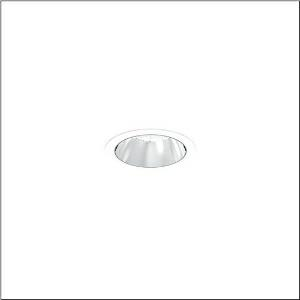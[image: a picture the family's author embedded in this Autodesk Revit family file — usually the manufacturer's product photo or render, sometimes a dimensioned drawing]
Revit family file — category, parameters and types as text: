
# Revit family: lunis_21_m_51db15mc91c
name_source: partatom
category: Lighting Fixtures
units: mm (PartAtom-declared; Revit-internal decimal feet)

## family parameters
Cut with Voids When Loaded = No
Host = Face
Light Source = No
Part Type = Normal
Room Calculation Point = No
Round Connector Dimension = Use Diameter
Shared = No

## types (1)
- --- (1 x LED, 4040 lm, 25.5 W, 6500K)
    Apparent Load = 26 VA
    CIE Flux Codes = 95 99 100 100 100
    Color Rendering = 80
    Color Temperature = 6500K
    Default Elevation = 1800 mm
    Description = Lunis 21,  M, downlight, light control with lens, of PMMA, anti glare with reflector, of PC, highly specular, light emission: direct distribution, LED rated luminous flux: 1.860lm, light colour: 830/840/865, with terminal, 3-pole, mains connection: 220..240V, AC/DC, 0/50..60Hz, housing, round, of diecast aluminium, traffic white (RAL 9016), diameter: 115mm, clamping range: 1..40mm, protection rating (complete): IP20, protection rating (on room side): IP54, insulation class (complete): insulation class II (safety insulation), certification: CE, impact resistance: IK03, packaging unit: 1 piece
    Height = 0 mm  [stored 0 ft]
    Lamp = 1 x LED
    Lamp Light Flux = 4040 lm
    Lamp Power = 25.5 W
    Lamp count = 1
    Length = 115 mm
    Luminous efficacy = 158 lm/W
    Manufacturer = Siteco
    ModVariant = No
    Model = 51DB15MC91C
    Mounting Place = Ceiling
    Mounting Type = Recessed
    Number of Poles = 1
    OnlyDefault = Yes
    Power Factor = 1
    Product Name = Lunis 21 M
    Product group = downlight
    ProductGroupID = 401
    Protection Class = Protection class II
    Protection Degree = IP 20
    RLX_Detail_Level = 1
    RLX_Emergency_Light_Flux = 0 lm
    RLX_Emergency_Type = 0
    RLX_Emergency_Type_DB = No
    RlxData = <blob elided: 14897 chars, md5=ce5ecd81>
    Socket = socket
    Standby Power = 0 W
    System Light Flux = 4040 lm
    System Power = 26 W
    Type Comments = individual setting: colour temperature 6500K, luminous flux: 100 % | (ON | ON | OFF | OFF) | 700 mA
    Type Image = l_1290850.jpg
    URL = http://relux.com
    VarID = @adj_040647
    Voltage = 0 V
    Weight = 0.00 kg
    Width = 0 mm  [stored 0 ft]

note: [stored X ft] marks values corroborated as IEEE doubles in the binary element streams (Revit-internal decimal feet)

## geometry (parser evidence)
native form markers: Sweep x10
no freeform markers — native parametric forms only
